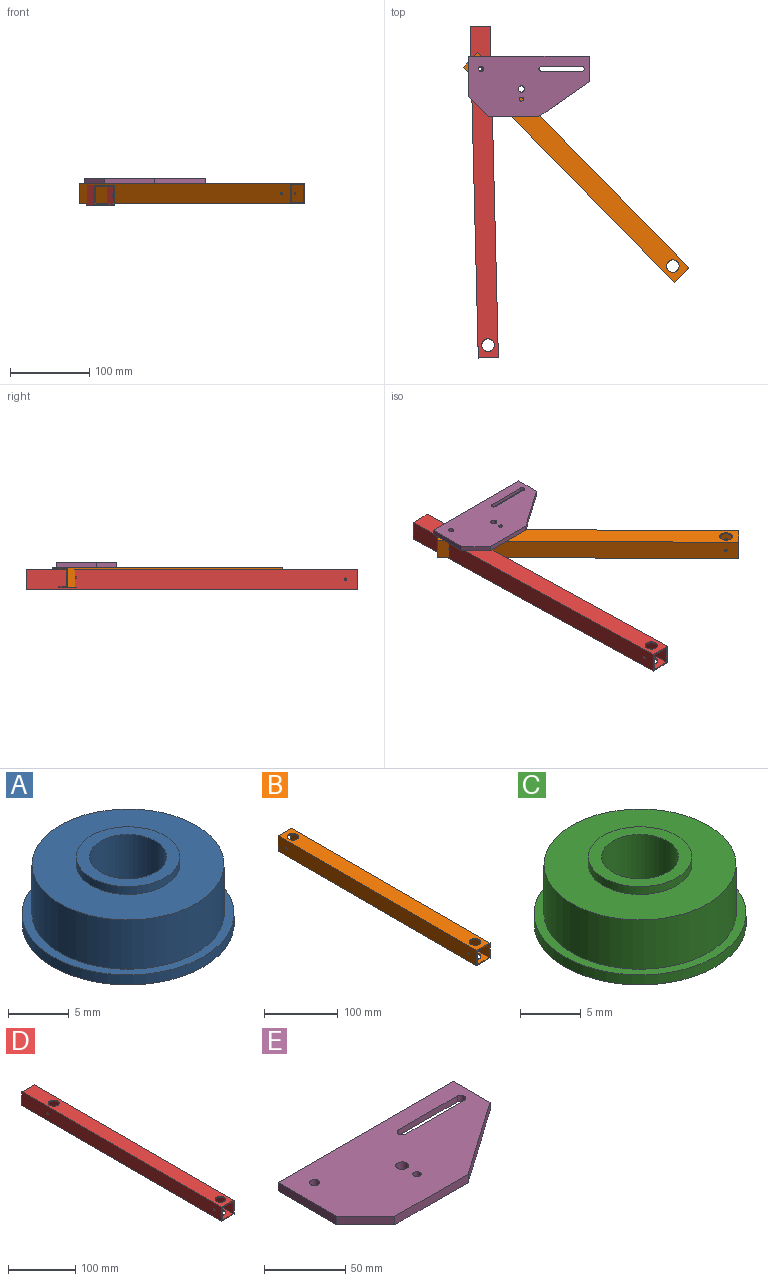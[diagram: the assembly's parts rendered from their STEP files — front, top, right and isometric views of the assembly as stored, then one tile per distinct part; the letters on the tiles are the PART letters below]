
ASSEMBLY  parts=5 mates=4
PART A: 10 faces, bbox 17.5x17.5x7.6 mm
  f0: cylinder r=3.17mm len=7.58mm, axis (0,0,1), area 151.2mm2, adj f7,f9
  f1: cylinder r=8.76mm len=17.53mm, axis (0,0,1), area 55.9mm2, adj f2,f3
  f2: plane 17.53x17.53mm, normal (0,0,-1), area 183.7mm2, adj f1,f8
  f3: plane 17.53x17.53mm, normal (0,0,1), area 43.3mm2, adj f1,f4
  f4: cylinder r=7.94mm len=15.88mm, axis (0,0,-1), area 248.3mm2, adj f3,f5
  f5: plane 15.88x15.88mm, normal (0,0,1), area 140.4mm2, adj f4,f6
  f6: cylinder r=4.28mm len=8.56mm, axis (0,0,-1), area 21.3mm2, adj f5,f7
  f7: plane 8.56x8.56mm, normal (0,0,1), area 25.9mm2, adj f0,f6
  f8: cylinder r=4.28mm len=8.56mm, axis (0,0,1), area 21.3mm2, adj f2,f9
  f9: plane 8.56x8.56mm, normal (0,0,-1), area 25.9mm2, adj f0,f8
PART B: 18 faces, bbox 25.4x381x25.4 mm
  f0: plane 381x25.4mm, normal (0,0,-1), area 9281.5mm2, adj f4,f7,f8,f9,f12,f13
  f1: plane 381x25.4mm, normal (0,0,1), area 9281.5mm2, adj f4,f7,f8,f9,f10,f11
  f2: plane 381x22.23mm, normal (0,0,1), area 8071.9mm2, adj f5,f6,f8,f9,f12,f13
  f3: plane 381x22.23mm, normal (0,0,-1), area 8071.9mm2, adj f5,f6,f8,f9,f10,f11
  f4: plane 381x25.4mm, normal (1,0,0), area 9661.6mm2, adj f0,f1,f8,f9,f16,f17
  f5: plane 381x22.23mm, normal (1,0,0), area 8451.9mm2, adj f2,f3,f8,f9,f14,f15
  f6: plane 381x22.23mm, normal (-1,0,0), area 8451.9mm2, adj f2,f3,f8,f9,f16,f17
  f7: plane 381x25.4mm, normal (-1,0,0), area 9661.6mm2, adj f0,f1,f8,f9,f14,f15
  f8: plane 25.4x25.4mm, normal (0,1,0), area 151.2mm2, adj f0,f1,f2,f3,f4,f5,f6,f7
  f9: plane 25.4x25.4mm, normal (0,-1,0), area 151.2mm2, adj f0,f1,f2,f3,f4,f5,f6,f7
  f10: cylinder r=7.94mm len=15.88mm, axis (0,0,-1), area 79.2mm2, adj f1,f3
  f11: cylinder r=7.94mm len=15.88mm, axis (0,0,-1), area 79.2mm2, adj f1,f3
  f12: cylinder r=7.94mm len=15.88mm, axis (0,0,-1), area 79.2mm2, adj f0,f2
  f13: cylinder r=7.94mm len=15.88mm, axis (0,0,-1), area 79.2mm2, adj f0,f2
  f14: cylinder r=1.59mm len=3.18mm, axis (-1,0,0), area 15.8mm2, adj f5,f7
  f15: cylinder r=1.59mm len=3.18mm, axis (-1,0,0), area 15.8mm2, adj f5,f7
  f16: cylinder r=1.59mm len=3.18mm, axis (-1,0,0), area 15.8mm2, adj f4,f6
  f17: cylinder r=1.59mm len=3.18mm, axis (-1,0,0), area 15.8mm2, adj f4,f6
PART C: 10 faces, bbox 17.5x17.5x7.6 mm
  f0: cylinder r=3.17mm len=7.58mm, axis (0,0,1), area 151.2mm2, adj f7,f9
  f1: cylinder r=8.76mm len=17.53mm, axis (0,0,1), area 55.9mm2, adj f2,f3
  f2: plane 17.53x17.53mm, normal (0,0,-1), area 183.7mm2, adj f1,f8
  f3: plane 17.53x17.53mm, normal (0,0,1), area 43.3mm2, adj f1,f4
  f4: cylinder r=7.94mm len=15.88mm, axis (0,0,-1), area 248.3mm2, adj f3,f5
  f5: plane 15.88x15.88mm, normal (0,0,1), area 140.4mm2, adj f4,f6
  f6: cylinder r=4.28mm len=8.56mm, axis (0,0,-1), area 21.3mm2, adj f5,f7
  f7: plane 8.56x8.56mm, normal (0,0,1), area 25.9mm2, adj f0,f6
  f8: cylinder r=4.28mm len=8.56mm, axis (0,0,1), area 21.3mm2, adj f2,f9
  f9: plane 8.56x8.56mm, normal (0,0,-1), area 25.9mm2, adj f0,f8
PART D: 18 faces, bbox 25.4x419.1x25.4 mm
  f0: plane 419.1x25.4mm, normal (0,0,-1), area 10249.3mm2, adj f1,f7,f8,f11,f12,f17
  f1: plane 419.1x25.4mm, normal (1,0,0), area 10629.3mm2, adj f0,f2,f8,f15,f16,f17
  f2: plane 419.1x25.4mm, normal (0,0,1), area 10249.3mm2, adj f1,f7,f8,f9,f10,f17
  f3: plane 419.1x22.23mm, normal (-1,0,0), area 9298.7mm2, adj f4,f6,f8,f15,f16,f17
  f4: plane 419.1x22.23mm, normal (0,0,1), area 8918.6mm2, adj f3,f5,f8,f11,f12,f17
  f5: plane 419.1x22.23mm, normal (1,0,0), area 9298.7mm2, adj f4,f6,f8,f13,f14,f17
  f6: plane 419.1x22.23mm, normal (0,0,-1), area 8918.6mm2, adj f3,f5,f8,f9,f10,f17
  f7: plane 419.1x25.4mm, normal (-1,0,0), area 10629.3mm2, adj f0,f2,f8,f13,f14,f17
  f8: plane 25.4x25.4mm, normal (0,-1,0), area 151.2mm2, adj f0,f1,f2,f3,f4,f5,f6,f7
  f9: cylinder r=7.94mm len=15.88mm, axis (0,0,-1), area 79.2mm2, adj f2,f6
  f10: cylinder r=7.94mm len=15.88mm, axis (0,0,-1), area 79.2mm2, adj f2,f6
  f11: cylinder r=7.94mm len=15.88mm, axis (0,0,-1), area 79.2mm2, adj f0,f4
  f12: cylinder r=7.94mm len=15.88mm, axis (0,0,-1), area 79.2mm2, adj f0,f4
  f13: cylinder r=1.59mm len=3.18mm, axis (-1,0,0), area 15.8mm2, adj f5,f7
  f14: cylinder r=1.59mm len=3.18mm, axis (-1,0,0), area 15.8mm2, adj f5,f7
  f15: cylinder r=1.59mm len=3.18mm, axis (-1,0,0), area 15.8mm2, adj f1,f3
  f16: cylinder r=1.59mm len=3.18mm, axis (-1,0,0), area 15.8mm2, adj f1,f3
  f17: plane 25.4x25.4mm, normal (0,1,0), area 151.2mm2, adj f0,f1,f2,f3,f4,f5,f6,f7
PART E: 20 faces, bbox 152.4x76.2x6.4 mm
  f0: plane 50.8x4.45mm, normal (0,-1,0), area 225.8mm2, adj f1,f3,f8,f15
  f1: cylinder r=3.17mm len=6.35mm, axis (0,0,-1), area 44.3mm2, adj f0,f2,f8,f15
  f2: plane 50.8x4.45mm, normal (0,1,0), area 225.8mm2, adj f1,f3,f8,f15
  f3: cylinder r=3.17mm len=6.35mm, axis (0,0,-1), area 44.3mm2, adj f0,f2,f8,f15
  f4: plane 50.8x6.35mm, normal (-1,0,0), area 322.6mm2, adj f6,f8,f9,f12
  f5: plane 31.75x6.35mm, normal (1,0,0), area 201.6mm2, adj f6,f8,f9,f10
  f6: plane 152.4x6.35mm, normal (0,1,0), area 967.7mm2, adj f4,f5,f8,f9
  f7: cylinder r=3.17mm len=6.35mm, axis (0,0,-1), area 126.7mm2, adj f8,f9
  f8: plane 152.4x76.2mm, normal (0,0,1), area 9423.1mm2, adj f0,f1,f2,f3,f4,f5,f6,f7
  f9: plane 152.4x76.2mm, normal (0,0,-1), area 8989.4mm2, adj f4,f5,f6,f7,f10,f11,f12,f13
  f10: plane 63.5x44.45mm, normal (0.57,-0.82,0), area 492.2mm2, adj f5,f8,f9,f11
  f11: plane 63.5x6.35mm, normal (0,-1,0), area 403.2mm2, adj f8,f9,f10,f12
  f12: plane 25.4x25.4mm, normal (-0.71,-0.71,0), area 228.1mm2, adj f4,f8,f9,f11
  f13: cylinder r=3.97mm len=7.94mm, axis (0,0,-1), area 158.3mm2, adj f8,f9
  f14: cylinder r=2.55mm len=6.35mm, axis (0,0,-1), area 101.8mm2, adj f8,f9
  f15: plane 64.77x12.7mm, normal (0,0,-1), area 433.7mm2, adj f0,f1,f2,f3,f16,f17,f18,f19
  f16: plane 52.07x1.91mm, normal (0,-1,0), area 99.2mm2, adj f9,f15,f17,f19
  f17: cylinder r=6.35mm len=12.7mm, axis (0,0,-1), area 38mm2, adj f9,f15,f16,f18
  f18: plane 52.07x1.91mm, normal (0,1,0), area 99.2mm2, adj f9,f15,f17,f19
  f19: cylinder r=6.35mm len=12.7mm, axis (0,0,-1), area 38mm2, adj f9,f15,f16,f18
PLACE A rot(axis=(-0.2,0.98,0),180deg) t=(135.99,47.31,-73.47)mm
PLACE B rot(axis=(-0.38,0.93,0),180deg) t=(166.27,69.03,-71.56)mm
PLACE C rot(axis=(-0.93,-0.36,0),180deg) t=(-259.86,670.48,-71.56)mm
PLACE D rot(axis=(0.01,-1,0),180deg) t=(8.98,1.36,-73.47)mm
PLACE E at identity fixed
MATE revolute A.f6 <-> E.f7  axis (0,0,1) through (-50.8,365.13,-39.91)mm
MATE pin_slot C.f8 <-> E.f1  axis (0,0,1) through (-53.33,365.13,-38)mm
MATE revolute D.f10 <-> A.f6  axis (0,0,1) through (-50.8,365.13,-41.72)mm
MATE revolute B.f10 <-> C.f8  axis (0,0,1) through (-53.33,365.13,-39.81)mm
